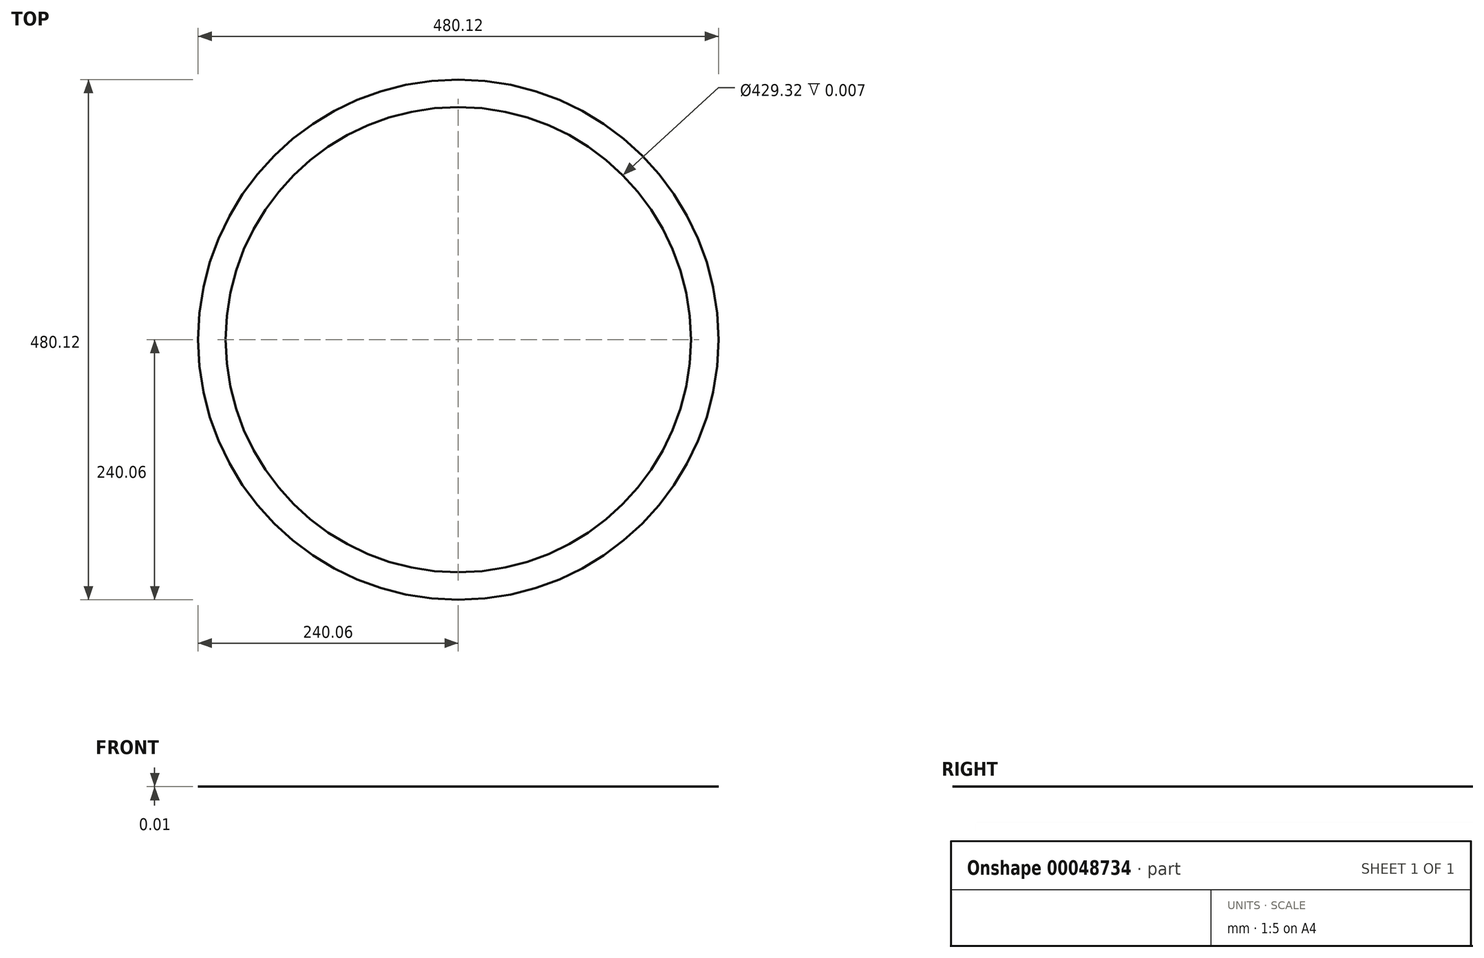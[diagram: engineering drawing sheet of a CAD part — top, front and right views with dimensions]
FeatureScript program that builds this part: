
annotation { "Feature Type Name" : "Feature", "Feature Type Description" : "" }
export const myFeature = defineFeature(function(context is Context, id is Id, definition is map)
    precondition{}
    {
        {
            var Q0;
            Q0=qCreatedBy(makeId("Top.planeOp"),FACE);
            var sketch = newSketch(context, id + "F0", { "sketchPlane" : qUnion([Q0])});
            skCircle(sketch, "E0", {"center": v(0, 0) * mm, "radius": 240.06 * mm});
            skCircle(sketch, "E1", {"center": v(0, 0) * mm, "radius": 214.66 * mm});
            skSolve(sketch);
        }
        {
            var Q0;
            Q0=makeQuery(id+"F0.imprint","IMPRINT",FACE,{"disambiguationData":[TD([[makeQuery(id+"F0.imprint","IMPRINT",EDGE,{"derivedFrom":sQuery(id+"F0.wireOp",EDGE,"E0")}),1.0]])]});
            extrude(context, id + "F1", {"entities" : qUnion([Q0]), "depth" : 3 / 406.4 * mm});
        }
    });
